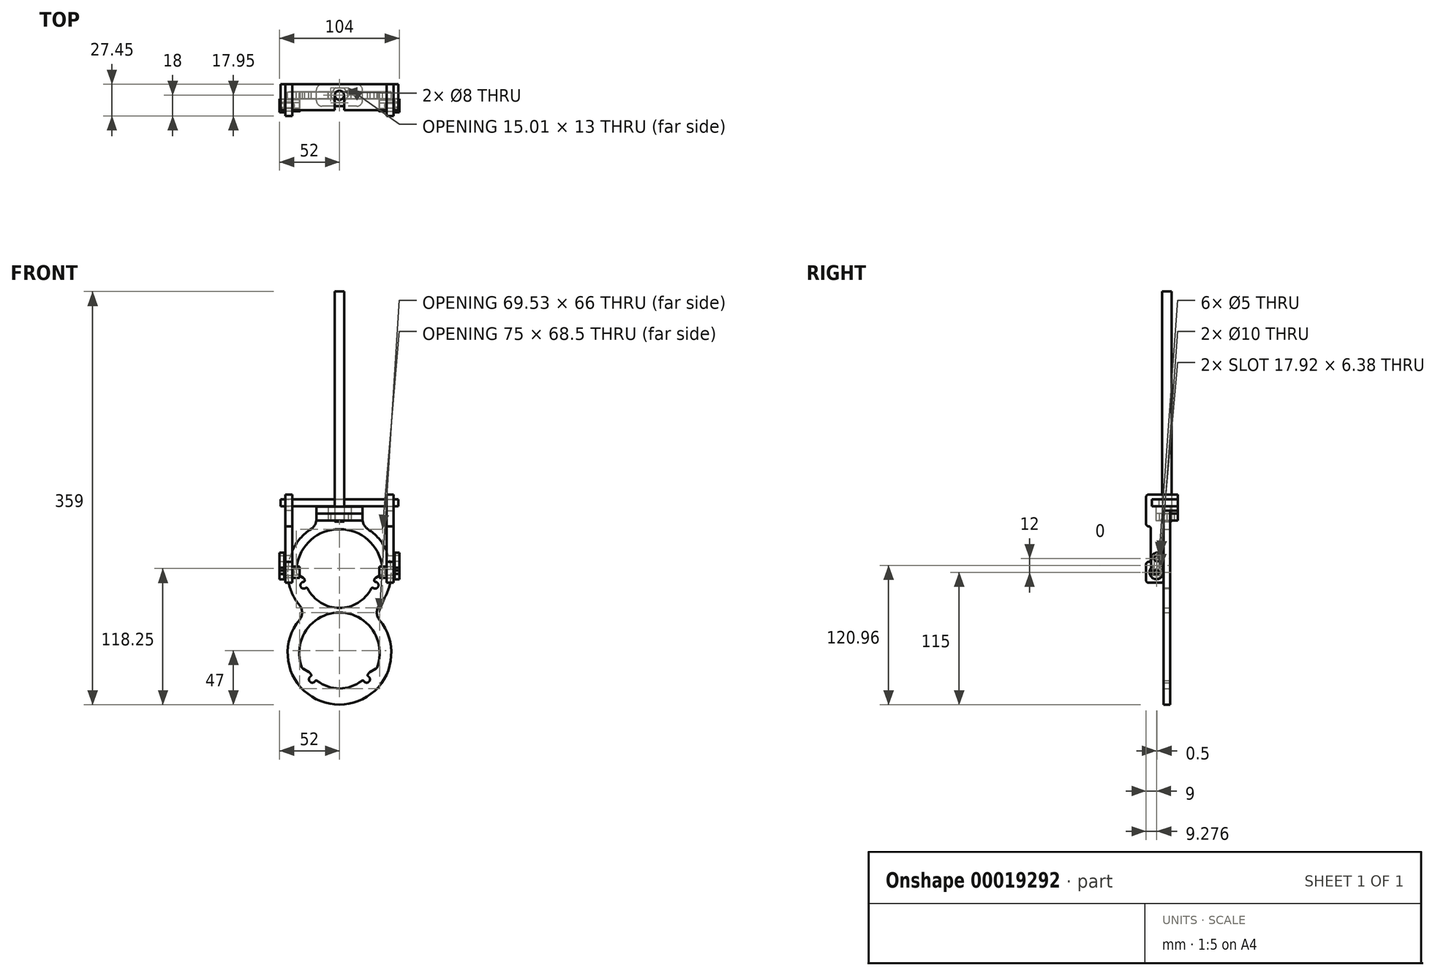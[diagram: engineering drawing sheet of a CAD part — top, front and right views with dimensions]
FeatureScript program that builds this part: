
annotation { "Feature Type Name" : "Feature", "Feature Type Description" : "" }
export const myFeature = defineFeature(function(context is Context, id is Id, definition is map)
    precondition{}
    {
        {
            var Q0;
            Q0=qCreatedBy(makeId("Front.planeOp"),FACE);
            var sketch = newSketch(context, id + "F0", { "sketchPlane" : qUnion([Q0])});
            skCircle(sketch, "E0", {"center": v(0, 0) * mm, "radius": 30 * mm, "construction": true});
            skArc(sketch, "E1", {"start": v(-29.8, -8.57) * mm, "mid": v(-33.82, -12.34) * mm, "end": v(-28.3, -12.64) * mm});
            skArc(sketch, "E2", {"start": v(-28.3, -12.64) * mm, "mid": v(0, -31) * mm, "end": v(28.3, -12.64) * mm});
            skArc(sketch, "E3.trimOffspring", {"start": v(29.8, -8.57) * mm, "mid": v(30.21, -6.95) * mm, "end": v(30.54, -5.31) * mm});
            skArc(sketch, "E4.trimOffspring", {"start": v(28.3, -12.64) * mm, "mid": v(33.82, -12.34) * mm, "end": v(29.8, -8.57) * mm});
            skArc(sketch, "E5.trimOffspring", {"start": v(34.92, 2.37) * mm, "mid": v(0, 35) * mm, "end": v(-34.92, 2.37) * mm});
            skArc(sketch, "E6", {"start": v(-34.92, 2.37) * mm, "mid": v(-33.89, -2.13) * mm, "end": v(-30.54, -5.31) * mm});
            skLineSegment(sketch, "E7", {"start": v(0, -11.31) * mm, "end": v(0, 0) * mm, "construction": true});
            skArc(sketch, "E8.0.MirrorCS", {"start": v(34.92, 2.37) * mm, "mid": v(33.89, -2.13) * mm, "end": v(30.54, -5.31) * mm});
            skArc(sketch, "E9.trimOffspring", {"start": v(-30.54, -5.31) * mm, "mid": v(-30.21, -6.95) * mm, "end": v(-29.8, -8.57) * mm});
            skLineSegment(sketch, "E10", {"start": v(-30.54, -5.31) * mm, "end": v(30.54, -5.31) * mm, "construction": true});
            skLineSegment(sketch, "E11", {"start": v(-31, -11.31) * mm, "end": v(31, -11.31) * mm, "construction": true});
            skLineSegment(sketch, "E12", {"start": v(-20, 57) * mm, "end": v(-10, 57) * mm});
            skLineSegment(sketch, "E13", {"start": v(20, 57) * mm, "end": v(20, 40.31) * mm});
            skLineSegment(sketch, "E14", {"start": v(-20, 57) * mm, "end": v(-20, 40.31) * mm});
            skPoint(sketch, "E15", {"position": v(0, 57) * mm});
            skArc(sketch, "E16", {"start": v(-20, 40.31) * mm, "mid": v(0, -45) * mm, "end": v(20, 40.31) * mm});
            skArc(sketch, "E17", {"start": v(20, 40.31) * mm, "mid": v(0, 45) * mm, "end": v(-20, 40.31) * mm, "construction": true});
            skLineSegment(sketch, "E18", {"start": v(-10, 57) * mm, "end": v(-10, 45) * mm});
            skLineSegment(sketch, "E19", {"start": v(10, 45) * mm, "end": v(10, 57) * mm});
            skLineSegment(sketch, "E20", {"start": v(-10, 45) * mm, "end": v(-4, 45) * mm});
            skLineSegment(sketch, "E21", {"start": v(10, 57) * mm, "end": v(20, 57) * mm});
            skLineSegment(sketch, "E22", {"start": v(-10, 57) * mm, "end": v(10, 57) * mm, "construction": true});
            skLineSegment(sketch, "E23", {"start": v(4, 45) * mm, "end": v(4, 44) * mm});
            skLineSegment(sketch, "E24", {"start": v(4, 44) * mm, "end": v(-4, 44) * mm});
            skLineSegment(sketch, "E25", {"start": v(-4, 44) * mm, "end": v(-4, 45) * mm});
            skLineSegment(sketch, "E26", {"start": v(4, 45) * mm, "end": v(10, 45) * mm});
            skLineSegment(sketch, "E27", {"start": v(-4, 45) * mm, "end": v(4, 45) * mm, "construction": true});
            skSolve(sketch);
        }
        {
            var Q0;
            Q0=qCreatedBy(makeId("Front.planeOp"),FACE);
            var sketch = newSketch(context, id + "F1", { "sketchPlane" : qUnion([Q0])});
            skArc(sketch, "E28.0", {"start": v(-20, 40.31) * mm, "mid": v(-44.73, 4.92) * mm, "end": v(-28.28, -35) * mm});
            skLineSegment(sketch, "E28.1", {"start": v(20, 57) * mm, "end": v(20, 40.31) * mm});
            skLineSegment(sketch, "E28.2", {"start": v(10, 57) * mm, "end": v(20, 57) * mm});
            skLineSegment(sketch, "E28.3", {"start": v(10, 45) * mm, "end": v(10, 57) * mm});
            skLineSegment(sketch, "E28.4", {"start": v(4, 45) * mm, "end": v(10, 45) * mm});
            skLineSegment(sketch, "E28.5", {"start": v(4, 45) * mm, "end": v(4, 44) * mm});
            skLineSegment(sketch, "E28.6", {"start": v(4, 44) * mm, "end": v(-4, 44) * mm});
            skLineSegment(sketch, "E28.7", {"start": v(-4, 44) * mm, "end": v(-4, 45) * mm});
            skLineSegment(sketch, "E28.8", {"start": v(-10, 45) * mm, "end": v(-4, 45) * mm});
            skLineSegment(sketch, "E28.9", {"start": v(-10, 57) * mm, "end": v(-10, 45) * mm});
            skLineSegment(sketch, "E28.10", {"start": v(-20, 57) * mm, "end": v(-10, 57) * mm});
            skLineSegment(sketch, "E28.11", {"start": v(-20, 57) * mm, "end": v(-20, 40.31) * mm});
            skCircle(sketch, "E29.0", {"center": v(0, 0) * mm, "radius": 30 * mm, "construction": true});
            skLineSegment(sketch, "E30", {"start": v(-37.5, 0) * mm, "end": v(37.5, 0) * mm, "construction": true});
            skLineSegment(sketch, "E31", {"start": v(-37.13, -5.24) * mm, "end": v(37.13, -5.24) * mm, "construction": true});
            skLineSegment(sketch, "E32", {"start": v(-35.78, -11.24) * mm, "end": v(35.78, -11.24) * mm, "construction": true});
            skLineSegment(sketch, "E33", {"start": v(0, 37.5) * mm, "end": v(0, -37.5) * mm, "construction": true});
            skLineSegment(sketch, "E34", {"start": v(-30.55, -5.24) * mm, "end": v(-37.48, -1.24) * mm});
            skLineSegment(sketch, "E35.0.MirrorCS", {"start": v(30.55, -5.24) * mm, "end": v(37.48, -1.24) * mm});
            skArc(sketch, "E36", {"start": v(30.55, -5.24) * mm, "mid": v(0, 31) * mm, "end": v(-30.55, -5.24) * mm, "construction": true});
            skArc(sketch, "E37", {"start": v(-30.55, -5.24) * mm, "mid": v(-30.22, -6.93) * mm, "end": v(-29.78, -8.6) * mm});
            skArc(sketch, "E38", {"start": v(-37.48, -1.24) * mm, "mid": v(0, -37.5) * mm, "end": v(37.48, -1.24) * mm, "construction": true});
            skArc(sketch, "E39", {"start": v(37.48, -1.24) * mm, "mid": v(0, 37.5) * mm, "end": v(-37.48, -1.24) * mm});
            skArc(sketch, "E40", {"start": v(29.78, -8.6) * mm, "mid": v(30.22, -6.93) * mm, "end": v(30.55, -5.24) * mm});
            skArc(sketch, "E41", {"start": v(28.38, -12.48) * mm, "mid": v(29.14, -10.56) * mm, "end": v(29.78, -8.6) * mm, "construction": true});
            skArc(sketch, "E42", {"start": v(-28.38, -12.48) * mm, "mid": v(0, -31) * mm, "end": v(28.38, -12.48) * mm});
            skArc(sketch, "E43", {"start": v(-29.78, -8.6) * mm, "mid": v(-29.14, -10.56) * mm, "end": v(-28.38, -12.48) * mm, "construction": true});
            skArc(sketch, "E44", {"start": v(-28.38, -12.48) * mm, "mid": v(-28.27, -10.25) * mm, "end": v(-29.78, -8.6) * mm, "construction": true});
            skArc(sketch, "E45", {"start": v(-29.78, -8.6) * mm, "mid": v(-33.73, -12.22) * mm, "end": v(-28.38, -12.48) * mm});
            skArc(sketch, "E46", {"start": v(28.38, -12.48) * mm, "mid": v(28.27, -10.25) * mm, "end": v(29.78, -8.6) * mm, "construction": true});
            skArc(sketch, "E47", {"start": v(29.78, -8.6) * mm, "mid": v(33.73, -12.22) * mm, "end": v(28.38, -12.48) * mm});
            skArc(sketch, "E48", {"start": v(-28.28, -35) * mm, "mid": v(0, -115) * mm, "end": v(28.28, -35) * mm});
            skArc(sketch, "E49", {"start": v(28.28, -35) * mm, "mid": v(0, -25) * mm, "end": v(-28.28, -35) * mm, "construction": true});
            skArc(sketch, "E50", {"start": v(28.28, -35) * mm, "mid": v(44.73, 4.92) * mm, "end": v(20, 40.31) * mm});
            skArc(sketch, "E51", {"start": v(-28.28, -35) * mm, "mid": v(0, -45) * mm, "end": v(28.28, -35) * mm, "construction": true});
            skCircle(sketch, "E52", {"center": v(0, -70) * mm, "radius": 30 * mm, "construction": true});
            skLineSegment(sketch, "E53", {"start": v(-35, -70) * mm, "end": v(35, -70) * mm, "construction": true});
            skLineSegment(sketch, "E54", {"start": v(0, -35) * mm, "end": v(0, -105) * mm, "construction": true});
            skLineSegment(sketch, "E55", {"start": v(-26.38, -93) * mm, "end": v(26.38, -93) * mm, "construction": true});
            skLineSegment(sketch, "E56", {"start": v(-30.6, -87) * mm, "end": v(30.6, -87) * mm, "construction": true});
            skLineSegment(sketch, "E57", {"start": v(-25.92, -87) * mm, "end": v(-32.39, -83.27) * mm});
            skArc(sketch, "E58", {"start": v(-25.92, -87) * mm, "mid": v(-24.8, -88.6) * mm, "end": v(-23.6, -90.1) * mm});
            skArc(sketch, "E59", {"start": v(25.92, -87) * mm, "mid": v(0, -39) * mm, "end": v(-25.92, -87) * mm, "construction": true});
            skLineSegment(sketch, "E60.0.MirrorCS", {"start": v(25.92, -87) * mm, "end": v(32.39, -83.27) * mm});
            skArc(sketch, "E61", {"start": v(-32.39, -83.27) * mm, "mid": v(0, -105) * mm, "end": v(32.39, -83.27) * mm, "construction": true});
            skArc(sketch, "E62", {"start": v(32.39, -83.27) * mm, "mid": v(0, -35) * mm, "end": v(-32.39, -83.27) * mm});
            skArc(sketch, "E63", {"start": v(-23.6, -90.1) * mm, "mid": v(-25.7, -95.03) * mm, "end": v(-20.72, -93.06) * mm});
            skArc(sketch, "E64", {"start": v(-20.72, -93.06) * mm, "mid": v(-21.54, -90.98) * mm, "end": v(-23.6, -90.1) * mm, "construction": true});
            skArc(sketch, "E65", {"start": v(23.6, -90.1) * mm, "mid": v(25.7, -95.03) * mm, "end": v(20.72, -93.06) * mm});
            skArc(sketch, "E66", {"start": v(20.72, -93.06) * mm, "mid": v(21.54, -90.98) * mm, "end": v(23.6, -90.1) * mm, "construction": true});
            skArc(sketch, "E67", {"start": v(23.6, -90.1) * mm, "mid": v(24.8, -88.6) * mm, "end": v(25.92, -87) * mm});
            skArc(sketch, "E68", {"start": v(20.72, -93.06) * mm, "mid": v(22.2, -91.63) * mm, "end": v(23.6, -90.1) * mm, "construction": true});
            skArc(sketch, "E69", {"start": v(-23.6, -90.1) * mm, "mid": v(-22.2, -91.63) * mm, "end": v(-20.72, -93.06) * mm, "construction": true});
            skArc(sketch, "E70", {"start": v(-20.72, -93.06) * mm, "mid": v(0, -101) * mm, "end": v(20.72, -93.06) * mm});
            skSolve(sketch);
        }
        {
            var Q0;
            Q0=qSketchRegion(id+"F1",true);
            extrude(context, id + "F2", {"entities" : qUnion([Q0]), "depth" : 6 * mm});
        }
        {
            var Q0;
            Q0=makeQuery(id+"F2.opExtrude","SWEPT_FACE",FACE,{"disambiguationData":[OSD([sQuery(id+"F1.wireOp",EDGE,"E28.4")])]});
            var sketch = newSketch(context, id + "F3", { "sketchPlane" : qUnion([Q0])});
            skLineSegment(sketch, "E71.bottom", {"start": v(20, -12.55) * mm, "end": v(-20, -12.55) * mm});
            skLineSegment(sketch, "E71.top", {"start": v(20, 6.45) * mm, "end": v(-20, 6.45) * mm});
            skLineSegment(sketch, "E71.left", {"start": v(20, -12.55) * mm, "end": v(20, -6.1) * mm});
            skLineSegment(sketch, "E71.right", {"start": v(-20, -12.55) * mm, "end": v(-20, -6.1) * mm});
            skCircle(sketch, "E72.cCircle", {"center": v(0, -3.05) * mm, "radius": 6.5 * mm, "construction": true});
            skLineSegment(sketch, "E72.0", {"start": v(-3.75, -9.55) * mm, "end": v(-7.5, -3.05) * mm});
            skLineSegment(sketch, "E72.1", {"start": v(-7.5, -3.05) * mm, "end": v(-3.75, 3.45) * mm});
            skLineSegment(sketch, "E72.2", {"start": v(-3.75, 3.45) * mm, "end": v(3.75, 3.45) * mm});
            skLineSegment(sketch, "E72.3", {"start": v(3.75, 3.45) * mm, "end": v(7.5, -3.05) * mm});
            skLineSegment(sketch, "E72.4", {"start": v(7.5, -3.05) * mm, "end": v(3.75, -9.55) * mm});
            skLineSegment(sketch, "E72.5", {"start": v(3.75, -9.55) * mm, "end": v(-3.75, -9.55) * mm});
            skPoint(sketch, "E72.0.midPoint", {"position": v(-5.63, -6.3) * mm});
            skLineSegment(sketch, "E73", {"start": v(10, -3.05) * mm, "end": v(-10, -3.05) * mm, "construction": true});
            skLineSegment(sketch, "E74", {"start": v(-10, 0) * mm, "end": v(-10, -6) * mm});
            skLineSegment(sketch, "E75.trimOffspring", {"start": v(20, 0) * mm, "end": v(20, 6.45) * mm});
            skLineSegment(sketch, "E76", {"start": v(-20, 0) * mm, "end": v(-10, 0) * mm});
            skLineSegment(sketch, "E77", {"start": v(-10, 0) * mm, "end": v(-10, -6.1) * mm});
            skLineSegment(sketch, "E78", {"start": v(-10, -6.1) * mm, "end": v(-20, -6.1) * mm});
            skLineSegment(sketch, "E79.trimOffspring", {"start": v(-20, 0) * mm, "end": v(-20, 6.45) * mm});
            skLineSegment(sketch, "E80", {"start": v(20, -6.1) * mm, "end": v(10, -6.1) * mm});
            skLineSegment(sketch, "E81", {"start": v(10, -6.1) * mm, "end": v(10, 0) * mm});
            skLineSegment(sketch, "E82", {"start": v(10, 0) * mm, "end": v(20, 0) * mm});
            skSolve(sketch);
        }
        {
            var Q0;
            Q0=qSketchRegion(id+"F3",true);
            extrude(context, id + "F4", {"entities" : qUnion([Q0]), "depth" : 6 * mm});
        }
        {
            var Q0;
            Q0=makeQuery(id+"F4.opExtrude","CAP_FACE",FACE,{"disambiguationData":[OSD([sQuery(id+"F3.wireOp",EDGE,"E71.bottom"),sQuery(id+"F3.wireOp",EDGE,"E71.top"),sQuery(id+"F3.wireOp",EDGE,"E71.left"),sQuery(id+"F3.wireOp",EDGE,"E71.right"),sQuery(id+"F3.wireOp",EDGE,"E72.0"),sQuery(id+"F3.wireOp",EDGE,"E72.1"),sQuery(id+"F3.wireOp",EDGE,"E72.2"),sQuery(id+"F3.wireOp",EDGE,"E72.3"),sQuery(id+"F3.wireOp",EDGE,"E72.4"),sQuery(id+"F3.wireOp",EDGE,"E72.5"),sQuery(id+"F3.wireOp",EDGE,"E75.trimOffspring"),sQuery(id+"F3.wireOp",EDGE,"E76"),sQuery(id+"F3.wireOp",EDGE,"E77"),sQuery(id+"F3.wireOp",EDGE,"E78"),sQuery(id+"F3.wireOp",EDGE,"E79.trimOffspring"),sQuery(id+"F3.wireOp",EDGE,"E80"),sQuery(id+"F3.wireOp",EDGE,"E81"),sQuery(id+"F3.wireOp",EDGE,"E82")])],"isStart":false});
            var sketch = newSketch(context, id + "F5", { "sketchPlane" : qUnion([Q0])});
            skLineSegment(sketch, "E83", {"start": v(20, -12.55) * mm, "end": v(20, -6.1) * mm});
            skLineSegment(sketch, "E84", {"start": v(20, -6.1) * mm, "end": v(10, -6.1) * mm});
            skLineSegment(sketch, "E85", {"start": v(10, -6.1) * mm, "end": v(10, 0) * mm});
            skLineSegment(sketch, "E86", {"start": v(10, 0) * mm, "end": v(20, 0) * mm});
            skLineSegment(sketch, "E87", {"start": v(20, 0) * mm, "end": v(20, 6.45) * mm});
            skLineSegment(sketch, "E88", {"start": v(20, 6.45) * mm, "end": v(-20, 6.45) * mm});
            skLineSegment(sketch, "E89", {"start": v(-20, 6.45) * mm, "end": v(-20, 0) * mm});
            skLineSegment(sketch, "E90", {"start": v(-20, 0) * mm, "end": v(-10, 0) * mm});
            skLineSegment(sketch, "E91", {"start": v(-10, 0) * mm, "end": v(-10, -6.1) * mm});
            skLineSegment(sketch, "E92", {"start": v(-10, -6.1) * mm, "end": v(-20, -6.1) * mm});
            skLineSegment(sketch, "E93", {"start": v(-20, -6.1) * mm, "end": v(-20, -12.55) * mm});
            skLineSegment(sketch, "E94", {"start": v(-20, -12.55) * mm, "end": v(20, -12.55) * mm});
            skCircle(sketch, "E95", {"center": v(0, -3) * mm, "radius": 4 * mm});
            skSolve(sketch);
        }
        {
            var Q0;
            Q0=qSketchRegion(id+"F5",true);
            extrude(context, id + "F6", {"entities" : qUnion([Q0]), "depth" : 6 * mm});
        }
        {
            var Q0;
            Q0=makeQuery(id+"F2.opExtrude","SWEPT_FACE",FACE,{"disambiguationData":[OSD([sQuery(id+"F1.wireOp",EDGE,"E28.6")])]});
            var sketch = newSketch(context, id + "F7", { "sketchPlane" : qUnion([Q0])});
            skCircle(sketch, "E96.0", {"center": v(0, -3) * mm, "radius": 4 * mm});
            skSolve(sketch);
        }
        {
            var Q0;
            Q0=qSketchRegion(id+"F7",true);
            extrude(context, id + "F8", {"entities" : qUnion([Q0]), "depth" : 200 * mm});
        }
        {
            var Q0;
            Q0=makeQuery(id+"F8.opExtrude","CAP_EDGE",EDGE,{"disambiguationData":[OSD([sQuery(id+"F7.wireOp",EDGE,"E96.0")])],"isStart":true});
            fillet(context, id + "F9", {"entities" : qUnion([Q0]), "radius" : 1 * mm, "tangentPropagation" : true, "allowEdgeOverflow" : false});
        }
        {
            var Q0;
            Q0=makeQuery(id+"F4.opExtrude","CAP_FACE",FACE,{"disambiguationData":[OSD([sQuery(id+"F3.wireOp",EDGE,"E71.bottom"),sQuery(id+"F3.wireOp",EDGE,"E71.top"),sQuery(id+"F3.wireOp",EDGE,"E71.left"),sQuery(id+"F3.wireOp",EDGE,"E71.right"),sQuery(id+"F3.wireOp",EDGE,"E72.0"),sQuery(id+"F3.wireOp",EDGE,"E72.1"),sQuery(id+"F3.wireOp",EDGE,"E72.2"),sQuery(id+"F3.wireOp",EDGE,"E72.3"),sQuery(id+"F3.wireOp",EDGE,"E72.4"),sQuery(id+"F3.wireOp",EDGE,"E72.5"),sQuery(id+"F3.wireOp",EDGE,"E75.trimOffspring"),sQuery(id+"F3.wireOp",EDGE,"E76"),sQuery(id+"F3.wireOp",EDGE,"E77"),sQuery(id+"F3.wireOp",EDGE,"E78"),sQuery(id+"F3.wireOp",EDGE,"E79.trimOffspring"),sQuery(id+"F3.wireOp",EDGE,"E80"),sQuery(id+"F3.wireOp",EDGE,"E81"),sQuery(id+"F3.wireOp",EDGE,"E82")])],"isStart":true});
            var sketch = newSketch(context, id + "F10", { "sketchPlane" : qUnion([Q0])});
            skLineSegment(sketch, "E97.0", {"start": v(-3.75, -3.45) * mm, "end": v(3.75, -3.45) * mm});
            skLineSegment(sketch, "E97.1", {"start": v(3.75, -3.45) * mm, "end": v(7.5, 3.05) * mm});
            skLineSegment(sketch, "E97.2", {"start": v(7.5, 3.05) * mm, "end": v(3.75, 9.55) * mm});
            skLineSegment(sketch, "E97.3", {"start": v(3.75, 9.55) * mm, "end": v(-3.75, 9.55) * mm});
            skLineSegment(sketch, "E97.4", {"start": v(-3.75, 9.55) * mm, "end": v(-7.5, 3.05) * mm});
            skLineSegment(sketch, "E97.5", {"start": v(-7.5, 3.05) * mm, "end": v(-3.75, -3.45) * mm});
            skCircle(sketch, "E98", {"center": v(0, 3) * mm, "radius": 4 * mm});
            skSolve(sketch);
        }
        {
            var Q0;
            Q0=qSketchRegion(id+"F10",true);
            extrude(context, id + "F11", {"entities" : qUnion([Q0]), "oppositeDirection" : true, "depth" : 6 * mm});
        }
        {
            var Q0;
            Q0=makeQuery(id+"F11.opExtrude","CAP_FACE",FACE,{"disambiguationData":[OSD([sQuery(id+"F10.wireOp",EDGE,"E97.0"),sQuery(id+"F10.wireOp",EDGE,"E97.1"),sQuery(id+"F10.wireOp",EDGE,"E97.2"),sQuery(id+"F10.wireOp",EDGE,"E97.3"),sQuery(id+"F10.wireOp",EDGE,"E97.4"),sQuery(id+"F10.wireOp",EDGE,"E97.5"),sQuery(id+"F10.wireOp",EDGE,"E98")])],"isStart":true});
            fillet(context, id + "F12", {"entities" : qUnion([Q0]), "radius" : .5 * mm, "tangentPropagation" : true, "allowEdgeOverflow" : false});
        }
        {
            var Q0;
            Q0=makeQuery(id+"F2.opExtrude","SWEPT_EDGE",EDGE,{"disambiguationData":[OSD([sQuery(id+"F1.wireOp",EDGE,"7ef6ca21-ba91-41a4-be12-a81d28838a3f.0.1.7"),sQuery(id+"F1.wireOp",EDGE,"8cea311c-6731-4f5f-bcff-866d9017b7052")])]});
            var Q1;
            Q1=makeQuery(id+"F2.opExtrude","SWEPT_EDGE",EDGE,{"disambiguationData":[OSD([sQuery(id+"F1.wireOp",EDGE,"7ef6ca21-ba91-41a4-be12-a81d28838a3f.0.1.6"),sQuery(id+"F1.wireOp",EDGE,"7ef6ca21-ba91-41a4-be12-a81d28838a3f.0.1.7")])]});
            var Q2;
            Q2=makeQuery(id+"F2.opExtrude","SWEPT_EDGE",EDGE,{"disambiguationData":[OSD([sQuery(id+"F1.wireOp",EDGE,"7ef6ca21-ba91-41a4-be12-a81d28838a3f.0.1.1"),sQuery(id+"F1.wireOp",EDGE,"7ef6ca21-ba91-41a4-be12-a81d28838a3f.0.1.2")])]});
            var Q3;
            Q3=makeQuery(id+"F2.opExtrude","SWEPT_EDGE",EDGE,{"disambiguationData":[OSD([sQuery(id+"F1.wireOp",EDGE,"7ef6ca21-ba91-41a4-be12-a81d28838a3f.0.1.1"),sQuery(id+"F1.wireOp",EDGE,"8cea311c-6731-4f5f-bcff-866d9017b7052")])]});
            var Q4;
            Q4=makeQuery(id+"F2.opExtrude","SWEPT_EDGE",EDGE,{"disambiguationData":[OSD([sQuery(id+"F1.wireOp",EDGE,"E35.0.MirrorCS"),sQuery(id+"F1.wireOp",EDGE,"E40")])]});
            var Q5;
            Q5=makeQuery(id+"F2.opExtrude","SWEPT_EDGE",EDGE,{"disambiguationData":[OSD([sQuery(id+"F1.wireOp",EDGE,"E35.0.MirrorCS"),sQuery(id+"F1.wireOp",EDGE,"E39")])]});
            var Q6;
            Q6=makeQuery(id+"F2.opExtrude","SWEPT_EDGE",EDGE,{"disambiguationData":[OSD([sQuery(id+"F1.wireOp",EDGE,"E34"),sQuery(id+"F1.wireOp",EDGE,"E37")])]});
            var Q7;
            Q7=makeQuery(id+"F2.opExtrude","SWEPT_EDGE",EDGE,{"disambiguationData":[OSD([sQuery(id+"F1.wireOp",EDGE,"E34"),sQuery(id+"F1.wireOp",EDGE,"E39")])]});
            var Q8;
            Q8=makeQuery(id+"F2.opExtrude","SWEPT_EDGE",EDGE,{"disambiguationData":[OSD([sQuery(id+"F1.wireOp",EDGE,"E57"),sQuery(id+"F1.wireOp",EDGE,"E62")])]});
            var Q9;
            Q9=makeQuery(id+"F2.opExtrude","SWEPT_EDGE",EDGE,{"disambiguationData":[OSD([sQuery(id+"F1.wireOp",EDGE,"E57"),sQuery(id+"F1.wireOp",EDGE,"E58")])]});
            var Q10;
            Q10=makeQuery(id+"F2.opExtrude","SWEPT_EDGE",EDGE,{"disambiguationData":[OSD([sQuery(id+"F1.wireOp",EDGE,"E60.0.MirrorCS"),sQuery(id+"F1.wireOp",EDGE,"E67")])]});
            var Q11;
            Q11=makeQuery(id+"F2.opExtrude","SWEPT_EDGE",EDGE,{"disambiguationData":[OSD([sQuery(id+"F1.wireOp",EDGE,"E60.0.MirrorCS"),sQuery(id+"F1.wireOp",EDGE,"E62")])]});
            fillet(context, id + "F13", {"entities" : qUnion([Q0, Q1, Q2, Q3, Q4, Q5, Q6, Q7, Q8, Q9, Q10, Q11]), "radius" : 2 * mm, "tangentPropagation" : true, "allowEdgeOverflow" : false});
        }
        {
            var Q0;
            Q0=makeQuery(id+"F2.opExtrude","SWEPT_EDGE",EDGE,{"disambiguationData":[OSD([sQuery(id+"F1.wireOp",EDGE,"E37"),sQuery(id+"F1.wireOp",EDGE,"E45")])]});
            var Q1;
            Q1=makeQuery(id+"F2.opExtrude","SWEPT_EDGE",EDGE,{"disambiguationData":[OSD([sQuery(id+"F1.wireOp",EDGE,"E42"),sQuery(id+"F1.wireOp",EDGE,"E45")])]});
            var Q2;
            Q2=makeQuery(id+"F2.opExtrude","SWEPT_EDGE",EDGE,{"disambiguationData":[OSD([sQuery(id+"F1.wireOp",EDGE,"E42"),sQuery(id+"F1.wireOp",EDGE,"E47")])]});
            var Q3;
            Q3=makeQuery(id+"F2.opExtrude","SWEPT_EDGE",EDGE,{"disambiguationData":[OSD([sQuery(id+"F1.wireOp",EDGE,"E40"),sQuery(id+"F1.wireOp",EDGE,"E47")])]});
            var Q4;
            Q4=makeQuery(id+"F2.opExtrude","SWEPT_EDGE",EDGE,{"disambiguationData":[OSD([sQuery(id+"F1.wireOp",EDGE,"7ef6ca21-ba91-41a4-be12-a81d28838a3f.0.1.5"),sQuery(id+"F1.wireOp",EDGE,"7ef6ca21-ba91-41a4-be12-a81d28838a3f.0.1.6")])]});
            var Q5;
            Q5=makeQuery(id+"F2.opExtrude","SWEPT_EDGE",EDGE,{"disambiguationData":[OSD([sQuery(id+"F1.wireOp",EDGE,"7ef6ca21-ba91-41a4-be12-a81d28838a3f.0.1.4"),sQuery(id+"F1.wireOp",EDGE,"7ef6ca21-ba91-41a4-be12-a81d28838a3f.0.1.5")])]});
            var Q6;
            Q6=makeQuery(id+"F2.opExtrude","SWEPT_EDGE",EDGE,{"disambiguationData":[OSD([sQuery(id+"F1.wireOp",EDGE,"7ef6ca21-ba91-41a4-be12-a81d28838a3f.0.1.3"),sQuery(id+"F1.wireOp",EDGE,"7ef6ca21-ba91-41a4-be12-a81d28838a3f.0.1.4")])]});
            var Q7;
            Q7=makeQuery(id+"F2.opExtrude","SWEPT_EDGE",EDGE,{"disambiguationData":[OSD([sQuery(id+"F1.wireOp",EDGE,"7ef6ca21-ba91-41a4-be12-a81d28838a3f.0.1.2"),sQuery(id+"F1.wireOp",EDGE,"7ef6ca21-ba91-41a4-be12-a81d28838a3f.0.1.3")])]});
            var Q8;
            Q8=makeQuery(id+"F2.opExtrude","SWEPT_EDGE",EDGE,{"disambiguationData":[OSD([sQuery(id+"F1.wireOp",EDGE,"E65"),sQuery(id+"F1.wireOp",EDGE,"E67")])]});
            var Q9;
            Q9=makeQuery(id+"F2.opExtrude","SWEPT_EDGE",EDGE,{"disambiguationData":[OSD([sQuery(id+"F1.wireOp",EDGE,"E65"),sQuery(id+"F1.wireOp",EDGE,"E70")])]});
            var Q10;
            Q10=makeQuery(id+"F2.opExtrude","SWEPT_EDGE",EDGE,{"disambiguationData":[OSD([sQuery(id+"F1.wireOp",EDGE,"E63"),sQuery(id+"F1.wireOp",EDGE,"E70")])]});
            var Q11;
            Q11=makeQuery(id+"F2.opExtrude","SWEPT_EDGE",EDGE,{"disambiguationData":[OSD([sQuery(id+"F1.wireOp",EDGE,"E58"),sQuery(id+"F1.wireOp",EDGE,"E63")])]});
            fillet(context, id + "F14", {"entities" : qUnion([Q0, Q1, Q2, Q3, Q4, Q5, Q6, Q7, Q8, Q9, Q10, Q11]), "radius" : 1.25 * mm, "tangentPropagation" : true, "allowEdgeOverflow" : false});
        }
        {
            var Q0;
            Q0=makeQuery(id+"F2.opExtrude","SWEPT_EDGE",EDGE,{"disambiguationData":[OSD([sQuery(id+"F1.wireOp",EDGE,"E28.0"),sQuery(id+"F1.wireOp",EDGE,"E28.11")])]});
            var Q1;
            Q1=makeQuery(id+"F2.opExtrude","SWEPT_EDGE",EDGE,{"disambiguationData":[OSD([sQuery(id+"F1.wireOp",EDGE,"E28.0"),sQuery(id+"F1.wireOp",EDGE,"E48")])]});
            var Q2;
            Q2=makeQuery(id+"F2.opExtrude","SWEPT_EDGE",EDGE,{"disambiguationData":[OSD([sQuery(id+"F1.wireOp",EDGE,"E28.1"),sQuery(id+"F1.wireOp",EDGE,"E50")])]});
            var Q3;
            Q3=makeQuery(id+"F2.opExtrude","SWEPT_EDGE",EDGE,{"disambiguationData":[OSD([sQuery(id+"F1.wireOp",EDGE,"E28.0"),sQuery(id+"F1.wireOp",EDGE,"E28.11")])]});
            var Q4;
            Q4=makeQuery(id+"F2.opExtrude","SWEPT_EDGE",EDGE,{"disambiguationData":[OSD([sQuery(id+"F1.wireOp",EDGE,"E48"),sQuery(id+"F1.wireOp",EDGE,"E50")])]});
            fillet(context, id + "F15", {"entities" : qUnion([Q0, Q1, Q2, Q3, Q4]), "radius" : 10 * mm, "tangentPropagation" : true, "allowEdgeOverflow" : false});
        }
        {
            var Q0;
            Q0=makeQuery(id+"F6.opExtrude","SWEPT_EDGE",EDGE,{"disambiguationData":[OSD([sQuery(id+"F5.wireOp",EDGE,"E93"),sQuery(id+"F5.wireOp",EDGE,"E94")])]});
            var Q1;
            Q1=makeQuery(id+"F4.opExtrude","SWEPT_EDGE",EDGE,{"disambiguationData":[OSD([sQuery(id+"F3.wireOp",EDGE,"E71.bottom"),sQuery(id+"F3.wireOp",EDGE,"E71.right")])]});
            var Q2;
            Q2=makeQuery(id+"F6.opExtrude","SWEPT_EDGE",EDGE,{"disambiguationData":[OSD([sQuery(id+"F5.wireOp",EDGE,"E88"),sQuery(id+"F5.wireOp",EDGE,"E89")])]});
            var Q3;
            Q3=makeQuery(id+"F4.opExtrude","SWEPT_EDGE",EDGE,{"disambiguationData":[OSD([sQuery(id+"F3.wireOp",EDGE,"E71.top"),sQuery(id+"F3.wireOp",EDGE,"E79.trimOffspring")])]});
            var Q4;
            Q4=makeQuery(id+"F6.opExtrude","SWEPT_EDGE",EDGE,{"disambiguationData":[OSD([sQuery(id+"F5.wireOp",EDGE,"E83"),sQuery(id+"F5.wireOp",EDGE,"E94")])]});
            var Q5;
            Q5=makeQuery(id+"F4.opExtrude","SWEPT_EDGE",EDGE,{"disambiguationData":[OSD([sQuery(id+"F3.wireOp",EDGE,"E71.bottom"),sQuery(id+"F3.wireOp",EDGE,"E71.left")])]});
            var Q6;
            Q6=makeQuery(id+"F6.opExtrude","SWEPT_EDGE",EDGE,{"disambiguationData":[OSD([sQuery(id+"F5.wireOp",EDGE,"E87"),sQuery(id+"F5.wireOp",EDGE,"E88")])]});
            var Q7;
            Q7=makeQuery(id+"F4.opExtrude","SWEPT_EDGE",EDGE,{"disambiguationData":[OSD([sQuery(id+"F3.wireOp",EDGE,"E71.top"),sQuery(id+"F3.wireOp",EDGE,"E75.trimOffspring")])]});
            fillet(context, id + "F16", {"entities" : qUnion([Q0, Q1, Q2, Q3, Q4, Q5, Q6, Q7]), "radius" : 5 * mm, "tangentPropagation" : true, "allowEdgeOverflow" : false});
        }
        {
            var Q0;
            Q0=makeQuery(id+"F2.opExtrude","CAP_FACE",FACE,{"disambiguationData":[OSD([sQuery(id+"F1.wireOp",EDGE,"E28.0"),sQuery(id+"F1.wireOp",EDGE,"E28.1"),sQuery(id+"F1.wireOp",EDGE,"E28.2"),sQuery(id+"F1.wireOp",EDGE,"E28.3"),sQuery(id+"F1.wireOp",EDGE,"E28.4"),sQuery(id+"F1.wireOp",EDGE,"E28.5"),sQuery(id+"F1.wireOp",EDGE,"E28.6"),sQuery(id+"F1.wireOp",EDGE,"E28.7"),sQuery(id+"F1.wireOp",EDGE,"E28.8"),sQuery(id+"F1.wireOp",EDGE,"E28.9"),sQuery(id+"F1.wireOp",EDGE,"E28.10"),sQuery(id+"F1.wireOp",EDGE,"E28.11"),sQuery(id+"F1.wireOp",EDGE,"E34"),sQuery(id+"F1.wireOp",EDGE,"E35.0.MirrorCS"),sQuery(id+"F1.wireOp",EDGE,"E37"),sQuery(id+"F1.wireOp",EDGE,"E39"),sQuery(id+"F1.wireOp",EDGE,"E40"),sQuery(id+"F1.wireOp",EDGE,"E42"),sQuery(id+"F1.wireOp",EDGE,"E45"),sQuery(id+"F1.wireOp",EDGE,"E47"),sQuery(id+"F1.wireOp",EDGE,"E48"),sQuery(id+"F1.wireOp",EDGE,"E50"),sQuery(id+"F1.wireOp",EDGE,"E57"),sQuery(id+"F1.wireOp",EDGE,"E58"),sQuery(id+"F1.wireOp",EDGE,"E60.0.MirrorCS"),sQuery(id+"F1.wireOp",EDGE,"E62"),sQuery(id+"F1.wireOp",EDGE,"E63"),sQuery(id+"F1.wireOp",EDGE,"E65"),sQuery(id+"F1.wireOp",EDGE,"E67"),sQuery(id+"F1.wireOp",EDGE,"E70")])],"isStart":false});
            var sketch = newSketch(context, id + "F17", { "sketchPlane" : qUnion([Q0])});
            skArc(sketch, "E99", {"start": v(44.73, -4.94) * mm, "mid": v(0, 45) * mm, "end": v(-44.73, -4.94) * mm});
            skArc(sketch, "E100", {"start": v(37.5, -0.08) * mm, "mid": v(0, 37.5) * mm, "end": v(-37.5, -0.08) * mm});
            skLineSegment(sketch, "E101", {"start": v(-37.5, -0.08) * mm, "end": v(-37.5, -4.94) * mm});
            skLineSegment(sketch, "E102", {"start": v(-37.5, -4.94) * mm, "end": v(-44.73, -4.94) * mm});
            skLineSegment(sketch, "E103", {"start": v(0, 25.85) * mm, "end": v(0, -12.58) * mm, "construction": true});
            skLineSegment(sketch, "E104.0.MirrorCS", {"start": v(37.5, -4.94) * mm, "end": v(44.73, -4.94) * mm});
            skLineSegment(sketch, "E105.0.MirrorCS", {"start": v(37.5, -0.08) * mm, "end": v(37.5, -4.94) * mm});
            skSolve(sketch);
        }
        {
            var Q0;
            Q0=qCreatedBy(makeId("Right.planeOp"),FACE);
            cPlane(context, id + "F18", {"entities" : qUnion([Q0]), "cplaneType" : CPlaneType.OFFSET, "offset" : 39 * mm, "oppositeDirection" : true, "width" : 150 * mm, "height" : 150 * mm});
        }
        {
            var Q0;
            Q0=qCreatedBy(id+"F18.planeOp",FACE);
            var sketch = newSketch(context, id + "F19", { "sketchPlane" : qUnion([Q0])});
            skCircle(sketch, "E106", {"center": v(-12, 0) * mm, "radius": 2.5 * mm});
            skSolve(sketch);
        }
        {
            var Q0;
            Q0=qSketchRegion(id+"F19",true);
            extrude(context, id + "F20", {"entities" : qUnion([Q0]), "operationType" : NewBodyOperationType.ADD, "oppositeDirection" : true, "depth" : 8 * mm});
        }
        {
            var Q0;
            Q0=makeQuery(id+"F20.opExtrude","CAP_FACE",FACE,{"disambiguationData":[OSD([sQuery(id+"F19.wireOp",EDGE,"E106")])],"isStart":false});
            var sketch = newSketch(context, id + "F21", { "sketchPlane" : qUnion([Q0])});
            skCircle(sketch, "E107", {"center": v(12, 0) * mm, "radius": 3 * mm});
            skSolve(sketch);
        }
        {
            var Q0;
            Q0=qSketchRegion(id+"F21",true);
            extrude(context, id + "F22", {"entities" : qUnion([Q0]), "operationType" : NewBodyOperationType.ADD, "depth" : 1 * mm});
        }
        {
            var Q0;
            Q0=makeQuery(id+"F20.opExtrude","CAP_EDGE",EDGE,{"disambiguationData":[OSD([sQuery(id+"F19.wireOp",EDGE,"E106")])],"isStart":true});
            fillet(context, id + "F23", {"entities" : qUnion([Q0]), "radius" : 2.5 * mm, "tangentPropagation" : true, "allowEdgeOverflow" : false});
        }
        {
            var Q0;
            Q0=makeQuery(id+"F22.opExtrude","CAP_FACE",FACE,{"disambiguationData":[OSD([sQuery(id+"F21.wireOp",EDGE,"E107")])],"isStart":true});
            var sketch = newSketch(context, id + "F24", { "sketchPlane" : qUnion([Q0])});
            skCircle(sketch, "E108", {"center": v(-12, 0) * mm, "radius": 2.5 * mm});
            skCircle(sketch, "E109", {"center": v(-12, 0) * mm, "radius": 5 * mm});
            skSolve(sketch);
        }
        {
            var Q0;
            Q0=qSketchRegion(id+"F24",true);
            extrude(context, id + "F25", {"entities" : qUnion([Q0]), "depth" : 12.5 * mm});
        }
        {
            var Q0;
            Q0=makeQuery(id+"F25.opExtrude","CAP_FACE",FACE,{"disambiguationData":[OSD([sQuery(id+"F24.wireOp",EDGE,"E108"),sQuery(id+"F24.wireOp",EDGE,"E109")])],"isStart":true});
            var sketch = newSketch(context, id + "F26", { "sketchPlane" : qUnion([Q0])});
            skLineSegment(sketch, "E110", {"start": v(6, -9) * mm, "end": v(21, -9) * mm});
            skLineSegment(sketch, "E111", {"start": v(21, -9) * mm, "end": v(21, 9) * mm});
            skLineSegment(sketch, "E112", {"start": v(21, 67.5) * mm, "end": v(-6.45, 67.5) * mm});
            skLineSegment(sketch, "E113", {"start": v(-6.45, 67.5) * mm, "end": v(-6.45, 63.5) * mm});
            skCircle(sketch, "E114", {"center": v(12, 0) * mm, "radius": 5 * mm});
            skLineSegment(sketch, "E115", {"start": v(-6.45, 63.5) * mm, "end": v(10, 63.5) * mm});
            skLineSegment(sketch, "E116", {"start": v(10, 63.5) * mm, "end": v(10, 57.5) * mm});
            skLineSegment(sketch, "E117", {"start": v(10, 57.5) * mm, "end": v(6, 57.5) * mm});
            skLineSegment(sketch, "E118.trimOffspring", {"start": v(6, 57.5) * mm, "end": v(6, 53.5) * mm, "construction": true});
            skLineSegment(sketch, "E119", {"start": v(21, 40) * mm, "end": v(17, 40) * mm});
            skLineSegment(sketch, "E120", {"start": v(17, 40) * mm, "end": v(17, 9) * mm});
            skLineSegment(sketch, "E121", {"start": v(17, 9) * mm, "end": v(21, 9) * mm});
            skLineSegment(sketch, "E122.trimOffspring", {"start": v(21, 40) * mm, "end": v(21, 67.5) * mm});
            skLineSegment(sketch, "E123", {"start": v(6, 57.5) * mm, "end": v(-6.45, 57.5) * mm});
            skLineSegment(sketch, "E124", {"start": v(-6.45, 57.5) * mm, "end": v(-6.45, 53.5) * mm});
            skLineSegment(sketch, "E125", {"start": v(-6.45, 53.5) * mm, "end": v(6, 53.5) * mm});
            skLineSegment(sketch, "E126", {"start": v(6, 53.5) * mm, "end": v(6, 53.5) * mm});
            skLineSegment(sketch, "E127", {"start": v(6, 53.5) * mm, "end": v(6, -9) * mm});
            skSolve(sketch);
        }
        {
            var Q0;
            Q0=qSketchRegion(id+"F26",true);
            extrude(context, id + "F27", {"entities" : qUnion([Q0]), "oppositeDirection" : true, "depth" : 6 * mm});
        }
        {
            var Q0;
            Q0=makeQuery(id+"F27.opExtrude","CAP_FACE",FACE,{"disambiguationData":[OSD([sQuery(id+"F26.wireOp",EDGE,"E110"),sQuery(id+"F26.wireOp",EDGE,"E111"),sQuery(id+"F26.wireOp",EDGE,"E112"),sQuery(id+"F26.wireOp",EDGE,"E113"),sQuery(id+"F26.wireOp",EDGE,"E114"),sQuery(id+"F26.wireOp",EDGE,"E115"),sQuery(id+"F26.wireOp",EDGE,"E116"),sQuery(id+"F26.wireOp",EDGE,"E117"),sQuery(id+"F26.wireOp",EDGE,"E118.trimOffspring"),sQuery(id+"F26.wireOp",EDGE,"E119"),sQuery(id+"F26.wireOp",EDGE,"E120"),sQuery(id+"F26.wireOp",EDGE,"E121"),sQuery(id+"F26.wireOp",EDGE,"E122.trimOffspring")])],"isStart":true});
            var sketch = newSketch(context, id + "F28", { "sketchPlane" : qUnion([Q0])});
            skCircle(sketch, "E128", {"center": v(11.5, 12) * mm, "radius": 2.5 * mm});
            skLineSegment(sketch, "E129", {"start": v(11.5, 12) * mm, "end": v(6, 12) * mm, "construction": true});
            skLineSegment(sketch, "E130", {"start": v(11.5, 12) * mm, "end": v(17, 12) * mm, "construction": true});
            skSolve(sketch);
        }
        {
            var Q0;
            Q0=makeQuery(id+"F28.imprint","IMPRINT",FACE,{"disambiguationData":[TD([[makeQuery(id+"F28.imprint","IMPRINT",EDGE,{"derivedFrom":sQuery(id+"F28.wireOp",EDGE,"E128")}),1.0]])]});
            extrude(context, id + "F29", {"entities" : qUnion([Q0]), "operationType" : NewBodyOperationType.REMOVE, "oppositeDirection" : true, "depth" : 25 * mm});
        }
        {
            var Q0;
            Q0=makeQuery(id+"F27.opExtrude","SWEPT_EDGE",EDGE,{"disambiguationData":[OSD([sQuery(id+"F26.wireOp",EDGE,"E119"),sQuery(id+"F26.wireOp",EDGE,"E122.trimOffspring")])]});
            var Q1;
            Q1=makeQuery(id+"F27.opExtrude","SWEPT_EDGE",EDGE,{"disambiguationData":[OSD([sQuery(id+"F26.wireOp",EDGE,"E112"),sQuery(id+"F26.wireOp",EDGE,"E122.trimOffspring")])]});
            var Q2;
            Q2=makeQuery(id+"F27.opExtrude","SWEPT_EDGE",EDGE,{"disambiguationData":[OSD([sQuery(id+"F26.wireOp",EDGE,"E111"),sQuery(id+"F26.wireOp",EDGE,"E121")])]});
            var Q3;
            Q3=makeQuery(id+"F27.opExtrude","SWEPT_EDGE",EDGE,{"disambiguationData":[OSD([sQuery(id+"F26.wireOp",EDGE,"E110"),sQuery(id+"F26.wireOp",EDGE,"E111")])]});
            var Q4;
            Q4=makeQuery(id+"F27.opExtrude","SWEPT_EDGE",EDGE,{"disambiguationData":[OSD([sQuery(id+"F26.wireOp",EDGE,"E110"),sQuery(id+"F26.wireOp",EDGE,"E118.trimOffspring")])]});
            var Q5;
            Q5=makeQuery(id+"F27.opExtrude","SWEPT_EDGE",EDGE,{"disambiguationData":[OSD([sQuery(id+"F26.wireOp",EDGE,"E119"),sQuery(id+"F26.wireOp",EDGE,"E120")])]});
            var Q6;
            Q6=makeQuery(id+"F27.opExtrude","SWEPT_EDGE",EDGE,{"disambiguationData":[OSD([sQuery(id+"F26.wireOp",EDGE,"E120"),sQuery(id+"F26.wireOp",EDGE,"E121")])]});
            fillet(context, id + "F30", {"entities" : qUnion([Q0, Q1, Q2, Q3, Q4, Q5, Q6]), "radius" : 2 * mm, "tangentPropagation" : true, "allowEdgeOverflow" : false});
        }
        {
            var Q0;
            Q0=makeQuery(id+"F27.opExtrude","CAP_FACE",FACE,{"disambiguationData":[OSD([sQuery(id+"F26.wireOp",EDGE,"E110"),sQuery(id+"F26.wireOp",EDGE,"E111"),sQuery(id+"F26.wireOp",EDGE,"E112"),sQuery(id+"F26.wireOp",EDGE,"E113"),sQuery(id+"F26.wireOp",EDGE,"E114"),sQuery(id+"F26.wireOp",EDGE,"E115"),sQuery(id+"F26.wireOp",EDGE,"E116"),sQuery(id+"F26.wireOp",EDGE,"E117"),sQuery(id+"F26.wireOp",EDGE,"E119"),sQuery(id+"F26.wireOp",EDGE,"E120"),sQuery(id+"F26.wireOp",EDGE,"E121"),sQuery(id+"F26.wireOp",EDGE,"E122.trimOffspring"),sQuery(id+"F26.wireOp",EDGE,"E123"),sQuery(id+"F26.wireOp",EDGE,"E124"),sQuery(id+"F26.wireOp",EDGE,"E125"),sQuery(id+"F26.wireOp",EDGE,"E127")])],"isStart":true});
            var sketch = newSketch(context, id + "F31", { "sketchPlane" : qUnion([Q0])});
            skArc(sketch, "E131", {"start": v(6.5, 2.4) * mm, "mid": v(12.93, -5.93) * mm, "end": v(16.5, 3.97) * mm});
            skArc(sketch, "E132", {"start": v(10, 2.24) * mm, "mid": v(12, -3) * mm, "end": v(14, 2.24) * mm});
            skLineSegment(sketch, "E133", {"start": v(10, 9.4) * mm, "end": v(10, 2.24) * mm});
            skLineSegment(sketch, "E134", {"start": v(14, 10.34) * mm, "end": v(14, 2.24) * mm});
            skArc(sketch, "E135", {"start": v(14, 10.34) * mm, "mid": v(10.81, 14.92) * mm, "end": v(10, 9.4) * mm});
            skLineSegment(sketch, "E136", {"start": v(6.5, 2.4) * mm, "end": v(6.5, 12) * mm});
            skLineSegment(sketch, "E137", {"start": v(16.5, 3.97) * mm, "end": v(16.5, 12) * mm});
            skArc(sketch, "E138", {"start": v(16.5, 12) * mm, "mid": v(11.5, 17) * mm, "end": v(6.5, 12) * mm});
            skSolve(sketch);
        }
        {
            var Q0;
            Q0=qSketchRegion(id+"F31",true);
            extrude(context, id + "F32", {"entities" : qUnion([Q0]), "depth" : 1 * mm});
        }
        {
            var Q0;
            Q0=makeQuery(id+"F32.opExtrude","CAP_FACE",FACE,{"disambiguationData":[OSD([sQuery(id+"F31.wireOp",EDGE,"E131"),sQuery(id+"F31.wireOp",EDGE,"E132"),sQuery(id+"F31.wireOp",EDGE,"E133"),sQuery(id+"F31.wireOp",EDGE,"E134"),sQuery(id+"F31.wireOp",EDGE,"E135"),sQuery(id+"F31.wireOp",EDGE,"E136"),sQuery(id+"F31.wireOp",EDGE,"E137"),sQuery(id+"F31.wireOp",EDGE,"E138")])],"isStart":false});
            var sketch = newSketch(context, id + "F33", { "sketchPlane" : qUnion([Q0])});
            skLineSegment(sketch, "E139.0.0", {"start": v(6.5, 12) * mm, "end": v(6.5, 2.4) * mm});
            skArc(sketch, "E139.0.1", {"start": v(6.5, 2.4) * mm, "mid": v(10.04, -5.67) * mm, "end": v(17.8, -1.5) * mm});
            skLineSegment(sketch, "E139.0.2", {"start": v(16.5, 3.97) * mm, "end": v(16.5, 12) * mm});
            skArc(sketch, "E139.0.3", {"start": v(16.5, 12) * mm, "mid": v(11.5, 17) * mm, "end": v(6.5, 12) * mm});
            skCircle(sketch, "E140", {"center": v(11.5, 12) * mm, "radius": 2.5 * mm});
            skArc(sketch, "E141", {"start": v(13.32, 1.5) * mm, "mid": v(10, 0) * mm, "end": v(13.32, -1.5) * mm});
            skLineSegment(sketch, "E142", {"start": v(13.32, 1.5) * mm, "end": v(17.8, 1.5) * mm});
            skLineSegment(sketch, "E143", {"start": v(13.32, -1.5) * mm, "end": v(17.8, -1.5) * mm});
            skArc(sketch, "E144.trimOffspring", {"start": v(17.8, 1.5) * mm, "mid": v(17.3, 2.81) * mm, "end": v(16.5, 3.97) * mm});
            skSolve(sketch);
        }
        {
            var Q0;
            Q0=qSketchRegion(id+"F33",true);
            extrude(context, id + "F34", {"entities" : qUnion([Q0]), "depth" : 4 * mm});
        }
        {
            var Q0;
            Q0=makeQuery(id+"F20.opExtrude","SWEPT_BODY",BODY,{"disambiguationData":[OSD([sQuery(id+"F19.wireOp",EDGE,"E106")])]});
            var Q1;
            Q1=makeQuery(id+"F25.opExtrude","SWEPT_BODY",BODY,{"disambiguationData":[OSD([sQuery(id+"F24.wireOp",EDGE,"E108"),sQuery(id+"F24.wireOp",EDGE,"E109")])]});
            var Q2;
            Q2=makeQuery(id+"F27.opExtrude","SWEPT_BODY",BODY,{"disambiguationData":[OSD([sQuery(id+"F26.wireOp",EDGE,"E110"),sQuery(id+"F26.wireOp",EDGE,"E111"),sQuery(id+"F26.wireOp",EDGE,"E112"),sQuery(id+"F26.wireOp",EDGE,"E113"),sQuery(id+"F26.wireOp",EDGE,"E114"),sQuery(id+"F26.wireOp",EDGE,"E115"),sQuery(id+"F26.wireOp",EDGE,"E116"),sQuery(id+"F26.wireOp",EDGE,"E117"),sQuery(id+"F26.wireOp",EDGE,"E118.trimOffspring"),sQuery(id+"F26.wireOp",EDGE,"E119"),sQuery(id+"F26.wireOp",EDGE,"E120"),sQuery(id+"F26.wireOp",EDGE,"E121"),sQuery(id+"F26.wireOp",EDGE,"E122.trimOffspring")])]});
            var Q3;
            Q3=makeQuery(id+"F34.opExtrude","SWEPT_BODY",BODY,{"disambiguationData":[OSD([sQuery(id+"F33.wireOp",EDGE,"E139.0.0"),sQuery(id+"F33.wireOp",EDGE,"E139.0.1"),sQuery(id+"F33.wireOp",EDGE,"E139.0.2"),sQuery(id+"F33.wireOp",EDGE,"E139.0.3"),sQuery(id+"F33.wireOp",EDGE,"E140"),sQuery(id+"F33.wireOp",EDGE,"E141"),sQuery(id+"F33.wireOp",EDGE,"E142"),sQuery(id+"F33.wireOp",EDGE,"E143"),sQuery(id+"F33.wireOp",EDGE,"E144.trimOffspring")])]});
            var Q4;
            Q4=makeQuery(id+"F32.opExtrude","SWEPT_BODY",BODY,{"disambiguationData":[OSD([sQuery(id+"F31.wireOp",EDGE,"E131"),sQuery(id+"F31.wireOp",EDGE,"E132"),sQuery(id+"F31.wireOp",EDGE,"E133"),sQuery(id+"F31.wireOp",EDGE,"E134"),sQuery(id+"F31.wireOp",EDGE,"E135"),sQuery(id+"F31.wireOp",EDGE,"E136"),sQuery(id+"F31.wireOp",EDGE,"E137"),sQuery(id+"F31.wireOp",EDGE,"E138")])]});
            var Q5;
            Q5=qCreatedBy(makeId("Right.planeOp"),FACE);
            mirror(context, id + "F35", {"entities" : qUnion([Q0, Q1, Q2, Q3, Q4]), "mirrorPlane" : qUnion([Q5])});
        }
        {
            var Q0;
            Q0=makeQuery(id+"F27.opExtrude","SWEPT_FACE",FACE,{"disambiguationData":[OSD([sQuery(id+"F26.wireOp",EDGE,"E117")])]});
            var sketch = newSketch(context, id + "F36", { "sketchPlane" : qUnion([Q0])});
            skLineSegment(sketch, "E145", {"start": v(-47, -10) * mm, "end": v(-47, -16) * mm});
            skLineSegment(sketch, "E146", {"start": v(-47, -16) * mm, "end": v(-51, -16) * mm});
            skLineSegment(sketch, "E147", {"start": v(-51, -16) * mm, "end": v(-51, 6.45) * mm});
            skLineSegment(sketch, "E148", {"start": v(-51, 6.45) * mm, "end": v(51, 6.45) * mm});
            skLineSegment(sketch, "E149", {"start": v(51, 6.45) * mm, "end": v(51, -16) * mm});
            skLineSegment(sketch, "E150", {"start": v(51, -16) * mm, "end": v(47, -16) * mm});
            skLineSegment(sketch, "E151", {"start": v(47, -16) * mm, "end": v(47, -10) * mm});
            skLineSegment(sketch, "E152", {"start": v(47, -10) * mm, "end": v(41, -10) * mm});
            skLineSegment(sketch, "E153", {"start": v(41, -10) * mm, "end": v(41, -16) * mm});
            skLineSegment(sketch, "E154", {"start": v(41, -16) * mm, "end": v(4, -16) * mm});
            skLineSegment(sketch, "E155", {"start": v(4, -16) * mm, "end": v(4, -3) * mm});
            skLineSegment(sketch, "E156", {"start": v(-4, -16) * mm, "end": v(-4, -3) * mm});
            skLineSegment(sketch, "E157", {"start": v(-4, -16) * mm, "end": v(-41, -16) * mm});
            skLineSegment(sketch, "E158", {"start": v(-41, -16) * mm, "end": v(-41, -10) * mm});
            skLineSegment(sketch, "E159", {"start": v(-41, -10) * mm, "end": v(-47, -10) * mm});
            skArc(sketch, "E160", {"start": v(4, -3) * mm, "mid": v(0, 1) * mm, "end": v(-4, -3) * mm});
            skSolve(sketch);
        }
        {
            var Q0;
            Q0=qSketchRegion(id+"F36",true);
            extrude(context, id + "F37", {"entities" : qUnion([Q0]), "depth" : 6 * mm});
        }
    });
